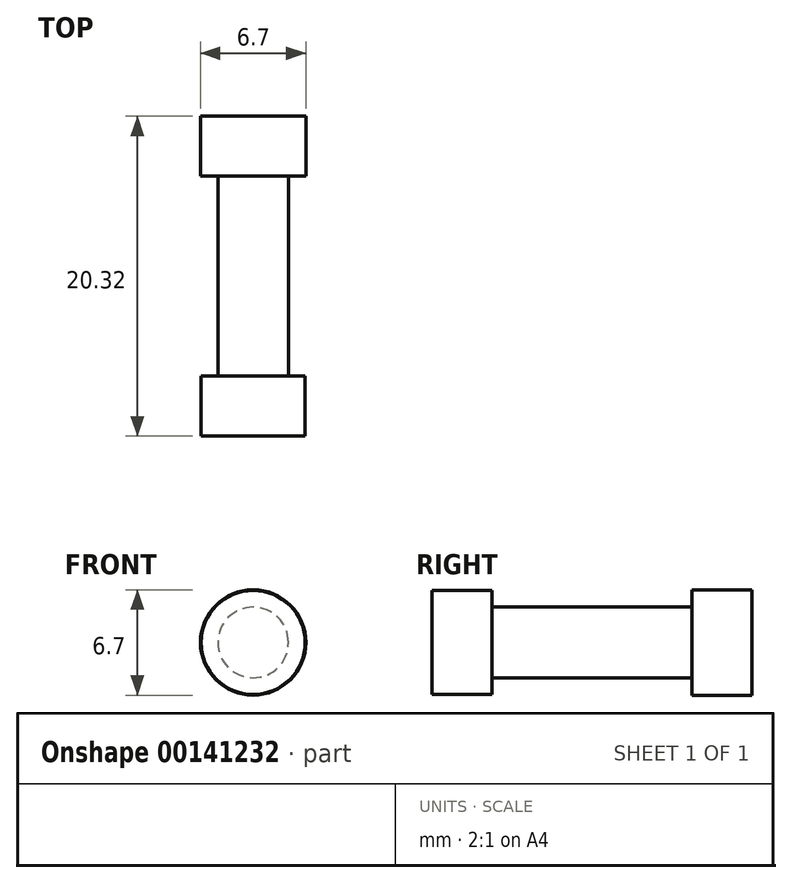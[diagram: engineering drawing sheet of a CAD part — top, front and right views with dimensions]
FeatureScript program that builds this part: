
annotation { "Feature Type Name" : "Feature", "Feature Type Description" : "" }
export const myFeature = defineFeature(function(context is Context, id is Id, definition is map)
    precondition{}
    {
        {
            var Q0;
            Q0=qCreatedBy(makeId("Front.planeOp"),FACE);
            var sketch = newSketch(context, id + "F0", { "sketchPlane" : qUnion([Q0])});
            skCircle(sketch, "E0", {"center": v(0, 0) * mm, "radius": 3.3 * mm});
            skSolve(sketch);
        }
        {
            var Q0;
            Q0 = qSketchRegion(id + "F0", true);
            extrude(context, id + "F1", {"entities" : qUnion([Q0]), "oppositeDirection" : true, "depth" : 3.8 * mm});
        }
        {
            var Q0;
            Q0=makeQuery(id+"F1.opExtrude","CAP_FACE",FACE,{"disambiguationData":[OSD([sQuery(id+"F0.wireOp",EDGE,"E0")])],"isStart":false});
            var sketch = newSketch(context, id + "F2", { "sketchPlane" : qUnion([Q0])});
            skCircle(sketch, "E1", {"center": v(0, 0) * mm, "radius": 2.24 * mm});
            skSolve(sketch);
        }
        {
            var Q0;
            Q0 = qSketchRegion(id + "F2", true);
            extrude(context, id + "F3", {"entities" : qUnion([Q0]), "operationType" : NewBodyOperationType.ADD, "depth" : 12.7 * mm});
        }
        {
            var Q0;
            Q0=makeQuery(id+"F3.opExtrude","CAP_FACE",FACE,{"disambiguationData":[OSD([sQuery(id+"F2.wireOp",EDGE,"E1")])],"isStart":false});
            var sketch = newSketch(context, id + "F4", { "sketchPlane" : qUnion([Q0])});
            skCircle(sketch, "E2", {"center": v(0, 0) * mm, "radius": 3.35 * mm});
            skSolve(sketch);
        }
        {
            var Q0;
            Q0 = qSketchRegion(id + "F4", true);
            extrude(context, id + "F5", {"entities" : qUnion([Q0]), "operationType" : NewBodyOperationType.ADD, "depth" : 3.8 * mm});
        }
    });
